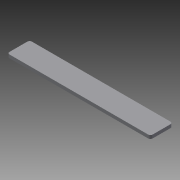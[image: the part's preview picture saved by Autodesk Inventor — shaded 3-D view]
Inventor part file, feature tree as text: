
AUTODESK INVENTOR PART (.ipt)
format: ipt  version: 2013 (Build 170138000, 138)  size: 74,752 bytes
history: native  units: in
note: dims shown in document units (in); Inventor stores cm internally (conversion verified against a paired STEP export)
features: extrude x1, sketch x1
ambient origin geometry x8: Origin, YZ Plane, XZ Plane, XY Plane, X Axis, Y Axis, Z Axis, Center Point
bodies: Solid1 (feature_tree)
feature tree (2):
  extrude  "Extrusion1"  Depth=5.0in
  sketch  "Sketch1"  dims[d0=32.0in d1=5.0in d2=0.5in d3=0.75in d4=0.0in]
